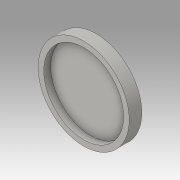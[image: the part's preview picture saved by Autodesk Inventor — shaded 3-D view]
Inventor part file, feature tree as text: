
AUTODESK INVENTOR PART (.ipt)
format: ipt  version: 2016 (Build 200138000, 138)  size: 89,600 bytes
history: native  units: in
note: dims shown in document units (in); Inventor stores cm internally (conversion verified against a paired STEP export)
features: extrude x1, shell x1, sketch x1
ambient origin geometry x8: Origin, YZ Plane, XZ Plane, XY Plane, X Axis, Y Axis, Z Axis, Center Point
bodies: Solid1 (feature_tree)
feature tree (3):
  extrude  "Extrusion1"  Depth=0.125in TaperAngle=0.0deg
  shell  "Shell1"  Thickness=0.1in
  sketch  "Sketch1"  dims[d0=1.425in d1=0.125in d2=0.0in d3=0.1in]
